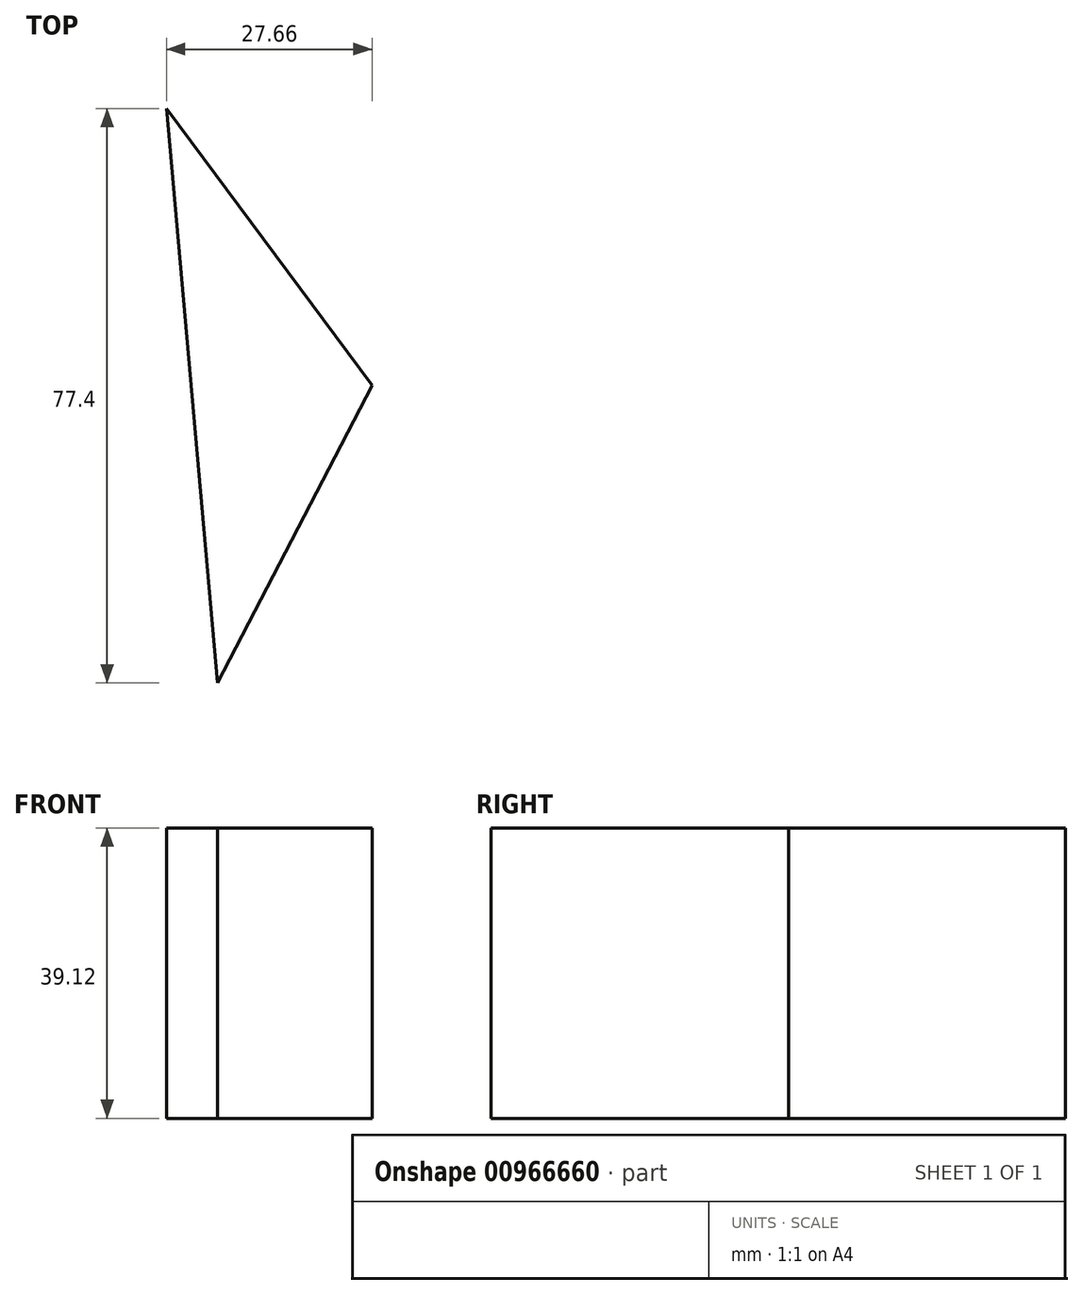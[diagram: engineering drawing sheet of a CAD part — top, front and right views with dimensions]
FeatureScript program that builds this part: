
annotation { "Feature Type Name" : "Feature", "Feature Type Description" : "" }
export const myFeature = defineFeature(function(context is Context, id is Id, definition is map)
    precondition{}
    {
        {
            var Q0;
            Q0=qCreatedBy(makeId("Top.planeOp"),FACE);
            var sketch = newSketch(context, id + "F0", { "sketchPlane" : qUnion([Q0])});
            skLineSegment(sketch, "E0", {"start": v(-100.83, -53.9) * mm, "end": v(-107.71, 23.5) * mm});
            skLineSegment(sketch, "E1", {"start": v(-107.71, 23.5) * mm, "end": v(-80.05, -13.81) * mm});
            skLineSegment(sketch, "E2", {"start": v(-80.05, -13.81) * mm, "end": v(-100.83, -53.9) * mm});
            skSolve(sketch);
        }
        {
            var Q0;
            Q0=makeQuery(id+"F0.imprint","IMPRINT",FACE,{"disambiguationData":[TD([[makeQuery(id+"F0.imprint","IMPRINT",EDGE,{"derivedFrom":sQuery(id+"F0.wireOp",EDGE,"E0")}),-1.0]])]});
            extrude(context, id + "F1", {"entities" : qUnion([Q0]), "depth" : 39.12 * mm, "offsetDistance" : 25.4 * mm});
        }
    });
